# Revit family: MP-A Series
name_source: partatom
category: Generic Models
revit_build: Autodesk Revit 2015 (Build: 20160512_0715(x64)
units: mm (PartAtom-declared; Revit-internal decimal feet)

## types (3) — shared parameters
Amp Only Width = 17.220"
Current Draw = 19.7
Default Elevation = 0.000"
Depth = 13.900"
Description = Multi-Channel Amplifier
Face Depth = 0.079"
Heat Load Active = 2191
Heat Load Standby = 7
Height = 1.750"
Manufacturer = QSC
Manufacturer URL = www.qsc.com
www.qsc.com
www.qsc.com
Model = MP-A80V
Power Active = 200
Product Documentation Link = https://www.qsc.com
Product Page URL = https://www.qsc.com
Regulatory Compliance = UL, CE, RoHS/WEEE, FCC Class B (conducted and radiated emissions)
Sustainability Rating = Energy Star
Voltage AC = 100-240 at 50-60 Hz
Weight Dimensional (kg) = 7.9
Weight Dimensional (lb) = 17.4
Weight Product (kg) = 5.8
Weight Product (lb) = 12.8
Width = 19.000"

## type names (no varying parameters)
- MP-A20V
- MP-A40V
- MP-A80V

## geometry (parser evidence)
native form markers: Blend x4, Sweep x9
no freeform markers — native parametric forms only
